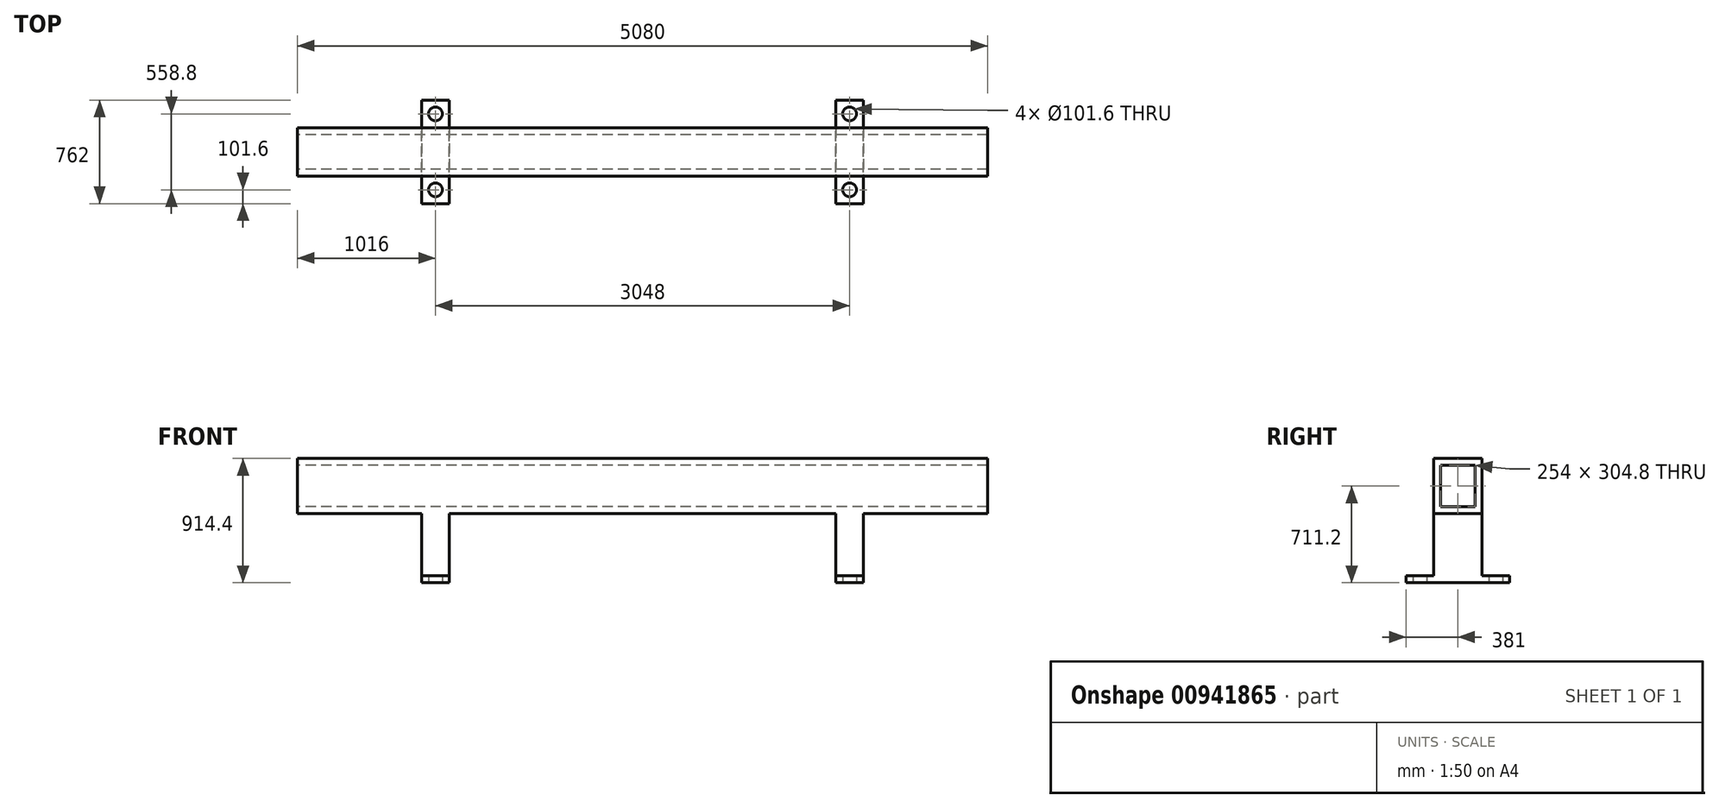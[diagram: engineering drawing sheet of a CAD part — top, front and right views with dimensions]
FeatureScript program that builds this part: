
annotation { "Feature Type Name" : "Feature", "Feature Type Description" : "" }
export const myFeature = defineFeature(function(context is Context, id is Id, definition is map)
    precondition{}
    {
        {
            var Q0;
            Q0=qCreatedBy(makeId("Top.planeOp"),FACE);
            var sketch = newSketch(context, id + "F0", { "sketchPlane" : qUnion([Q0])});
            skLineSegment(sketch, "E0.bottom", {"start": v(-2540, -177.8) * mm, "end": v(2540, -177.8) * mm});
            skLineSegment(sketch, "E0.top", {"start": v(-2540, 177.8) * mm, "end": v(2540, 177.8) * mm});
            skLineSegment(sketch, "E0.left", {"start": v(-2540, -177.8) * mm, "end": v(-2540, 177.8) * mm});
            skLineSegment(sketch, "E0.right", {"start": v(2540, -177.8) * mm, "end": v(2540, 177.8) * mm});
            skPoint(sketch, "E0.middle", {"position": v(0, 0) * mm});
            skLineSegment(sketch, "E1.bottom", {"start": v(-1625.6, -381) * mm, "end": v(-1422.4, -381) * mm});
            skLineSegment(sketch, "E1.top", {"start": v(-1625.6, 381) * mm, "end": v(-1422.4, 381) * mm});
            skLineSegment(sketch, "E1.left", {"start": v(-1625.6, -381) * mm, "end": v(-1625.6, 381) * mm});
            skLineSegment(sketch, "E1.right", {"start": v(-1422.4, -381) * mm, "end": v(-1422.4, 381) * mm});
            skPoint(sketch, "E1.middle", {"position": v(-1524, 0) * mm});
            skLineSegment(sketch, "E2.bottom", {"start": v(1422.4, -381) * mm, "end": v(1625.6, -381) * mm});
            skLineSegment(sketch, "E2.top", {"start": v(1422.4, 381) * mm, "end": v(1625.6, 381) * mm});
            skLineSegment(sketch, "E2.left", {"start": v(1422.4, -381) * mm, "end": v(1422.4, 381) * mm});
            skLineSegment(sketch, "E2.right", {"start": v(1625.6, -381) * mm, "end": v(1625.6, 381) * mm});
            skPoint(sketch, "E2.middle", {"position": v(1524, 0) * mm});
            skCircle(sketch, "E3", {"center": v(-1524, 279.4) * mm, "radius": 50.8 * mm});
            skCircle(sketch, "E4", {"center": v(-1524, -279.4) * mm, "radius": 50.8 * mm});
            skCircle(sketch, "E5", {"center": v(1524, 279.4) * mm, "radius": 50.8 * mm});
            skCircle(sketch, "E6", {"center": v(1524, -279.4) * mm, "radius": 50.8 * mm});
            skSolve(sketch);
        }
        {
            var Q0;
            {var subQ1=sQuery(id+"F0.wireOp",EDGE,"E1.top");Q0=makeQuery(id+"F0.imprint","IMPRINT",FACE,{"disambiguationData":[TD([[makeQuery(id+"F0.imprint","IMPRINT",EDGE,{"derivedFrom":subQ1}),-1.0]])]});}
            var Q1;
            {var subQ1=sQuery(id+"F0.wireOp",EDGE,"E1.bottom");Q1=makeQuery(id+"F0.imprint","IMPRINT",FACE,{"disambiguationData":[TD([[makeQuery(id+"F0.imprint","IMPRINT",EDGE,{"derivedFrom":subQ1}),1.0]])]});}
            var Q2;
            {var subQ0=sQuery(id+"F0.wireOp",EDGE,"E1.left");var subQ1=sQuery(id+"F0.wireOp",EDGE,"E0.bottom");var subQ2=makeQuery(id+"F0.imprint","INTERSECT",VERTEX,{"derivedFrom":[subQ1,subQ0]});Q2=makeQuery(id+"F0.imprint","IMPRINT",FACE,{"disambiguationData":[TD([[makeQuery(id+"F0.imprint","IMPRINT",EDGE,{"disambiguationData":[TD([[subQ2,-1.0]])],"derivedFrom":subQ1}),1.0]])]});}
            var Q3;
            {var subQ0=sQuery(id+"F0.wireOp",EDGE,"E1.right");var subQ1=sQuery(id+"F0.wireOp",EDGE,"E0.bottom");var subQ2=makeQuery(id+"F0.imprint","INTERSECT",VERTEX,{"derivedFrom":[subQ1,subQ0]});Q3=makeQuery(id+"F0.imprint","IMPRINT",FACE,{"disambiguationData":[TD([[makeQuery(id+"F0.imprint","IMPRINT",EDGE,{"disambiguationData":[TD([[subQ2,-1.0]])],"derivedFrom":subQ1}),1.0]])]});}
            var Q4;
            {var subQ0=sQuery(id+"F0.wireOp",EDGE,"E0.left");Q4=makeQuery(id+"F0.imprint","IMPRINT",FACE,{"disambiguationData":[TD([[makeQuery(id+"F0.imprint","IMPRINT",EDGE,{"derivedFrom":subQ0}),-1.0]])]});}
            var Q5;
            {var subQ0=sQuery(id+"F0.wireOp",EDGE,"E0.right");Q5=makeQuery(id+"F0.imprint","IMPRINT",FACE,{"disambiguationData":[TD([[makeQuery(id+"F0.imprint","IMPRINT",EDGE,{"derivedFrom":subQ0}),1.0]])]});}
            var Q6;
            {var subQ0=sQuery(id+"F0.wireOp",EDGE,"E2.left");var subQ1=sQuery(id+"F0.wireOp",EDGE,"E0.bottom");var subQ2=makeQuery(id+"F0.imprint","INTERSECT",VERTEX,{"derivedFrom":[subQ1,subQ0]});Q6=makeQuery(id+"F0.imprint","IMPRINT",FACE,{"disambiguationData":[TD([[makeQuery(id+"F0.imprint","IMPRINT",EDGE,{"disambiguationData":[TD([[subQ2,-1.0]])],"derivedFrom":subQ1}),1.0]])]});}
            var Q7;
            {var subQ1=sQuery(id+"F0.wireOp",EDGE,"E2.top");Q7=makeQuery(id+"F0.imprint","IMPRINT",FACE,{"disambiguationData":[TD([[makeQuery(id+"F0.imprint","IMPRINT",EDGE,{"derivedFrom":subQ1}),-1.0]])]});}
            var Q8;
            {var subQ1=sQuery(id+"F0.wireOp",EDGE,"E2.bottom");Q8=makeQuery(id+"F0.imprint","IMPRINT",FACE,{"disambiguationData":[TD([[makeQuery(id+"F0.imprint","IMPRINT",EDGE,{"derivedFrom":subQ1}),1.0]])]});}
            extrude(context, id + "F1", {"entities" : qUnion([Q0, Q1, Q2, Q3, Q4, Q5, Q6, Q7, Q8]), "depth" : 50.8 * mm, "offsetDistance" : 25.4 * mm});
        }
        {
            var Q0;
            {var subQ0=sQuery(id+"F0.wireOp",EDGE,"E1.right");var subQ1=sQuery(id+"F0.wireOp",EDGE,"E0.bottom");var subQ2=makeQuery(id+"F0.imprint","INTERSECT",VERTEX,{"derivedFrom":[subQ1,subQ0]});Q0=makeQuery(id+"F0.imprint","IMPRINT",FACE,{"disambiguationData":[TD([[makeQuery(id+"F0.imprint","IMPRINT",EDGE,{"disambiguationData":[TD([[subQ2,-1.0]])],"derivedFrom":subQ1}),1.0]])]});}
            var Q1;
            {var subQ0=sQuery(id+"F0.wireOp",EDGE,"E0.right");Q1=makeQuery(id+"F0.imprint","IMPRINT",FACE,{"disambiguationData":[TD([[makeQuery(id+"F0.imprint","IMPRINT",EDGE,{"derivedFrom":subQ0}),1.0]])]});}
            var Q2;
            {var subQ0=sQuery(id+"F0.wireOp",EDGE,"E0.left");Q2=makeQuery(id+"F0.imprint","IMPRINT",FACE,{"disambiguationData":[TD([[makeQuery(id+"F0.imprint","IMPRINT",EDGE,{"derivedFrom":subQ0}),-1.0]])]});}
            var Q3;
            {var subQ0=sQuery(id+"F0.wireOp",EDGE,"E1.left");var subQ1=sQuery(id+"F0.wireOp",EDGE,"E0.bottom");var subQ2=makeQuery(id+"F0.imprint","INTERSECT",VERTEX,{"derivedFrom":[subQ1,subQ0]});Q3=makeQuery(id+"F0.imprint","IMPRINT",FACE,{"disambiguationData":[TD([[makeQuery(id+"F0.imprint","IMPRINT",EDGE,{"disambiguationData":[TD([[subQ2,-1.0]])],"derivedFrom":subQ1}),1.0]])]});}
            var Q4;
            {var subQ0=sQuery(id+"F0.wireOp",EDGE,"E2.left");var subQ1=sQuery(id+"F0.wireOp",EDGE,"E0.bottom");var subQ2=makeQuery(id+"F0.imprint","INTERSECT",VERTEX,{"derivedFrom":[subQ1,subQ0]});Q4=makeQuery(id+"F0.imprint","IMPRINT",FACE,{"disambiguationData":[TD([[makeQuery(id+"F0.imprint","IMPRINT",EDGE,{"disambiguationData":[TD([[subQ2,-1.0]])],"derivedFrom":subQ1}),1.0]])]});}
            extrude(context, id + "F2", {"entities" : qUnion([Q0, Q1, Q2, Q3, Q4]), "operationType" : NewBodyOperationType.ADD, "depth" : 914.4 * mm, "offsetDistance" : 25.4 * mm});
        }
        {
            var Q0;
            {var subQ0=sQuery(id+"F0.wireOp",EDGE,"E0.left");Q0=makeQuery(id+"F2.boolean.opBoolean","MERGE",FACE,{"derivedFrom":[makeQuery(id+"F1.opExtrude","SWEPT_FACE",FACE,{"disambiguationData":[OSD([subQ0])]}),makeQuery(id+"F2.opExtrude","SWEPT_FACE",FACE,{"disambiguationData":[OSD([subQ0])]})]});}
            var sketch = newSketch(context, id + "F3", { "sketchPlane" : qUnion([Q0])});
            skLineSegment(sketch, "E7.bottom", {"start": v(-127, 558.8) * mm, "end": v(127, 558.8) * mm});
            skLineSegment(sketch, "E7.top", {"start": v(-127, 863.6) * mm, "end": v(127, 863.6) * mm});
            skLineSegment(sketch, "E7.left", {"start": v(-127, 558.8) * mm, "end": v(-127, 863.6) * mm});
            skLineSegment(sketch, "E7.right", {"start": v(127, 558.8) * mm, "end": v(127, 863.6) * mm});
            skPoint(sketch, "E7.middle", {"position": v(0, 711.2) * mm});
            skLineSegment(sketch, "E8.bottom", {"start": v(127, 863.6) * mm, "end": v(228.6, 863.6) * mm});
            skLineSegment(sketch, "E8.top", {"start": v(127, 711.2) * mm, "end": v(228.6, 711.2) * mm});
            skLineSegment(sketch, "E8.left", {"start": v(127, 863.6) * mm, "end": v(127, 711.2) * mm});
            skLineSegment(sketch, "E8.right", {"start": v(228.6, 863.6) * mm, "end": v(228.6, 711.2) * mm});
            skSolve(sketch);
        }
        {
            var Q0;
            Q0=makeQuery(id+"F3.imprint","IMPRINT",FACE,{"disambiguationData":[TD([[makeQuery(id+"F3.imprint","IMPRINT",EDGE,{"derivedFrom":sQuery(id+"F3.wireOp",EDGE,"E7.bottom")}),1.0]])]});
            var Q1;
            {var subQ0=sQuery(id+"F3.wireOp",EDGE,"E8.right");Q1=makeQuery(id+"F3.imprint","IMPRINT",FACE,{"disambiguationData":[TD([[makeQuery(id+"F3.imprint","IMPRINT",EDGE,{"derivedFrom":subQ0}),-1.0]])]});}
            var Q2;
            {var subQ0=sQuery(id+"F3.wireOp",EDGE,"E8.left");Q2=makeQuery(id+"F3.imprint","IMPRINT",FACE,{"disambiguationData":[TD([[makeQuery(id+"F3.imprint","IMPRINT",EDGE,{"derivedFrom":subQ0}),1.0]])]});}
            extrude(context, id + "F4", {"entities" : qUnion([Q0, Q1, Q2]), "operationType" : NewBodyOperationType.REMOVE, "oppositeDirection" : true, "depth" : 5963.92 * mm, "offsetDistance" : 25.4 * mm});
        }
        {
            var Q0;
            {var subQ2=sQuery(id+"F0.wireOp",EDGE,"E0.bottom");var subQ4=sQuery(id+"F0.wireOp",EDGE,"E1.right");var subQ6=makeQuery(id+"F0.imprint","INTERSECT",VERTEX,{"derivedFrom":[subQ2,subQ4]});var subQ7=sQuery(id+"F0.wireOp",EDGE,"E0.right");var subQ17=sQuery(id+"F0.wireOp",EDGE,"E0.left");Q0=makeQuery(id+"F4.boolean.opBoolean","SPLIT",FACE,{"disambiguationData":[TD([makeQuery(id+"F4.opExtrude","SWEPT_FACE",FACE,{"disambiguationData":[OSD([sQuery(id+"F3.wireOp",EDGE,"E8.top")])]})])],"derivedFrom":makeQuery(id+"F2.boolean.opBoolean","MERGE",FACE,{"derivedFrom":[makeQuery(id+"F1.opExtrude","SWEPT_FACE",FACE,{"disambiguationData":[OSD([subQ2]),TDD([makeQuery(id+"F0.imprint","IMPRINT",EDGE,{"disambiguationData":[TD([[makeQuery(id+"F0.imprint","INTERSECT",VERTEX,{"derivedFrom":[subQ2,subQ17]}),-1.0]])],"derivedFrom":subQ2})])]}),makeQuery(id+"F1.opExtrude","SWEPT_FACE",FACE,{"disambiguationData":[OSD([subQ2]),TDD([makeQuery(id+"F0.imprint","IMPRINT",EDGE,{"disambiguationData":[TD([[subQ6,-1.0]])],"derivedFrom":subQ2})])]}),makeQuery(id+"F1.opExtrude","SWEPT_FACE",FACE,{"disambiguationData":[OSD([subQ2]),TDD([makeQuery(id+"F0.imprint","IMPRINT",EDGE,{"disambiguationData":[TD([[makeQuery(id+"F0.imprint","INTERSECT",VERTEX,{"derivedFrom":[subQ2,subQ7]}),1.0]])],"derivedFrom":subQ2})])]}),makeQuery(id+"F2.opExtrude","SWEPT_FACE",FACE,{"disambiguationData":[OSD([subQ2])]})]})});}
            var sketch = newSketch(context, id + "F5", { "sketchPlane" : qUnion([Q0])});
            skLineSegment(sketch, "E9.bottom", {"start": v(-1625.6, 0) * mm, "end": v(-2540, 0) * mm});
            skLineSegment(sketch, "E9.top", {"start": v(-1625.6, 508) * mm, "end": v(-2540, 508) * mm});
            skLineSegment(sketch, "E9.left", {"start": v(-1625.6, 0) * mm, "end": v(-1625.6, 508) * mm});
            skLineSegment(sketch, "E9.right", {"start": v(-2540, 0) * mm, "end": v(-2540, 508) * mm});
            skLineSegment(sketch, "E10.bottom", {"start": v(-1422.4, 0) * mm, "end": v(1422.4, 0) * mm});
            skLineSegment(sketch, "E10.top", {"start": v(-1422.4, 508) * mm, "end": v(1422.4, 508) * mm});
            skLineSegment(sketch, "E10.left", {"start": v(-1422.4, 0) * mm, "end": v(-1422.4, 508) * mm});
            skLineSegment(sketch, "E10.right", {"start": v(1422.4, 0) * mm, "end": v(1422.4, 508) * mm});
            skLineSegment(sketch, "E11.bottom", {"start": v(1625.6, 0) * mm, "end": v(2540, 0) * mm});
            skLineSegment(sketch, "E11.top", {"start": v(1625.6, 508) * mm, "end": v(2540, 508) * mm});
            skLineSegment(sketch, "E11.left", {"start": v(1625.6, 0) * mm, "end": v(1625.6, 508) * mm});
            skLineSegment(sketch, "E11.right", {"start": v(2540, 0) * mm, "end": v(2540, 508) * mm});
            skSolve(sketch);
        }
        {
            var Q0;
            {var subQ1=sQuery(id+"F5.wireOp",EDGE,"E10.bottom");Q0=makeQuery(id+"F5.imprint","IMPRINT",FACE,{"disambiguationData":[TD([[makeQuery(id+"F5.imprint","IMPRINT",EDGE,{"derivedFrom":subQ1}),1.0]])]});}
            var Q1;
            {var subQ1=sQuery(id+"F5.wireOp",EDGE,"E11.bottom");Q1=makeQuery(id+"F5.imprint","IMPRINT",FACE,{"disambiguationData":[TD([[makeQuery(id+"F5.imprint","IMPRINT",EDGE,{"derivedFrom":subQ1}),1.0]])]});}
            var Q2;
            {var subQ1=sQuery(id+"F5.wireOp",EDGE,"E9.bottom");Q2=makeQuery(id+"F5.imprint","IMPRINT",FACE,{"disambiguationData":[TD([[makeQuery(id+"F5.imprint","IMPRINT",EDGE,{"derivedFrom":subQ1}),1.0]])]});}
            extrude(context, id + "F6", {"entities" : qUnion([Q0, Q1, Q2]), "operationType" : NewBodyOperationType.REMOVE, "oppositeDirection" : true, "depth" : 1143 * mm, "offsetDistance" : 25.4 * mm});
        }
    });
